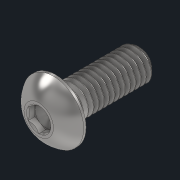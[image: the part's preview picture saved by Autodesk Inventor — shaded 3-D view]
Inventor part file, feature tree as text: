
AUTODESK INVENTOR PART (.ipt)
format: ipt  version: 2021 (Build 250183000, 183)  size: 564,736 bytes
history: native  units: in
note: dims shown in document units (in); Inventor stores cm internally (conversion verified against a paired STEP export)
features: revolve x1
ambient origin geometry x8: Origin, YZ Plane, XZ Plane, XY Plane, X Axis, Y Axis, Z Axis, Center Point
bodies: Solid1 (feature_tree)
feature tree (1):
  revolve  "Revolve2"  [1 undecoded]
note: 1 required parameter value undecoded (feature->parameter linkage not recoverable at this tier; creation-order binding heuristic only, values carry confidence <= 0.55)
